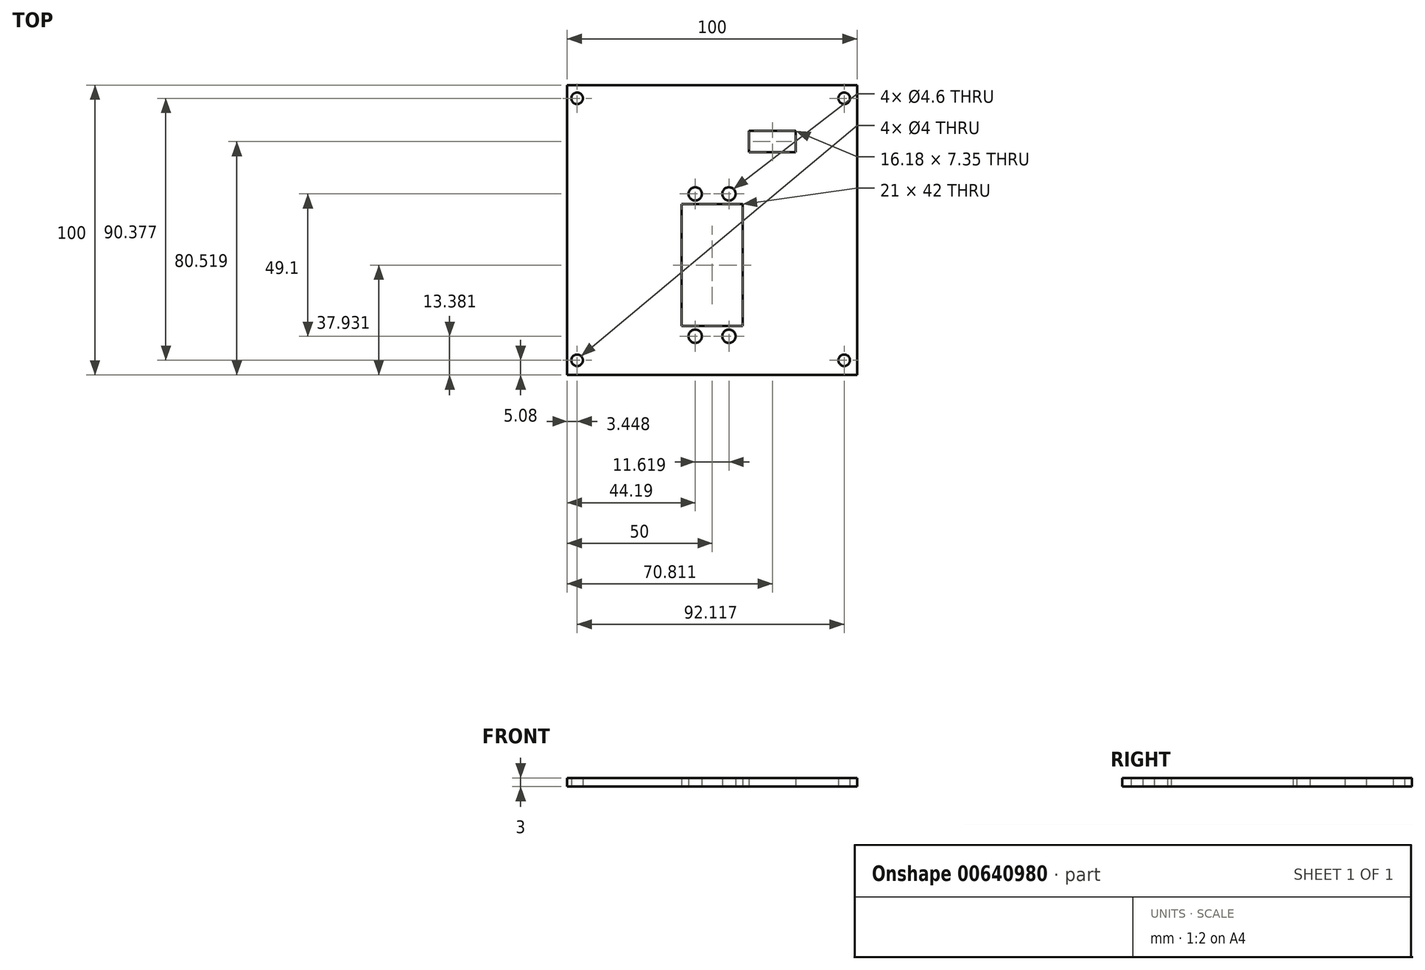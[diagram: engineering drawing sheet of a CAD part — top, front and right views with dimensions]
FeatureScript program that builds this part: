
annotation { "Feature Type Name" : "Feature", "Feature Type Description" : "" }
export const myFeature = defineFeature(function(context is Context, id is Id, definition is map)
    precondition{}
    {
        {
            var Q0;
            Q0=qCreatedBy(makeId("Top.planeOp"),FACE);
            var sketch = newSketch(context, id + "F0", { "sketchPlane" : qUnion([Q0])});
            skLineSegment(sketch, "E0.bottom", {"start": v(50, -50) * mm, "end": v(-50, -50) * mm});
            skLineSegment(sketch, "E0.top", {"start": v(50, 50) * mm, "end": v(-50, 50) * mm});
            skLineSegment(sketch, "E0.left", {"start": v(50, -50) * mm, "end": v(50, 50) * mm});
            skLineSegment(sketch, "E0.right", {"start": v(-50, -50) * mm, "end": v(-50, 50) * mm});
            skPoint(sketch, "E0.middle", {"position": v(0, 11.68) * mm});
            skLineSegment(sketch, "E1.bottom", {"start": v(10.5, -33.07) * mm, "end": v(-10.5, -33.07) * mm});
            skLineSegment(sketch, "E1.top", {"start": v(10.5, 8.93) * mm, "end": v(-10.5, 8.93) * mm});
            skLineSegment(sketch, "E1.left", {"start": v(10.5, -33.07) * mm, "end": v(10.5, 8.93) * mm});
            skLineSegment(sketch, "E1.right", {"start": v(-10.5, -33.07) * mm, "end": v(-10.5, 8.93) * mm});
            skPoint(sketch, "E1.middle", {"position": v(0, -12.07) * mm});
            skCircle(sketch, "E2", {"center": v(-5.8, 12.48) * mm, "radius": 2.3 * mm});
            skCircle(sketch, "E3.MirrorC", {"center": v(5.8, 12.48) * mm, "radius": 2.3 * mm});
            skLineSegment(sketch, "E4", {"start": v(28.9, -12.07) * mm, "end": v(-32.28, -12.07) * mm, "construction": true});
            skCircle(sketch, "E5.MirrorC", {"center": v(-5.8, -36.62) * mm, "radius": 2.3 * mm});
            skCircle(sketch, "E6.MirrorC", {"center": v(5.8, -36.62) * mm, "radius": 2.3 * mm});
            skPoint(sketch, "E7", {"position": v(-46.55, 45.46) * mm});
            skPoint(sketch, "E8.MirrorP", {"position": v(45.56, 45.46) * mm});
            skPoint(sketch, "E9", {"position": v(-46.55, -44.92) * mm});
            skPoint(sketch, "E10.MirrorP", {"position": v(45.56, -44.92) * mm});
            skLineSegment(sketch, "E11", {"start": v(-46.55, 45.46) * mm, "end": v(-46.55, -44.92) * mm, "construction": true});
            skLineSegment(sketch, "E12.bottom", {"start": v(12.72, 34.2) * mm, "end": v(28.9, 34.2) * mm});
            skLineSegment(sketch, "E12.top", {"start": v(12.72, 26.84) * mm, "end": v(28.9, 26.84) * mm});
            skLineSegment(sketch, "E12.left", {"start": v(12.72, 34.2) * mm, "end": v(12.72, 26.84) * mm});
            skLineSegment(sketch, "E12.right", {"start": v(28.9, 34.2) * mm, "end": v(28.9, 26.84) * mm});
            skSolve(sketch);
        }
        {
            var Q0;
            Q0=makeQuery(id+"F0.imprint","IMPRINT",FACE,{"disambiguationData":[TD([[makeQuery(id+"F0.imprint","IMPRINT",EDGE,{"derivedFrom":sQuery(id+"F0.wireOp",EDGE,"E0.bottom")}),-1.0]])]});
            extrude(context, id + "F1", {"entities" : qUnion([Q0]), "depth" : 3 * mm, "offsetDistance" : 25.4 * mm});
        }
        {
            var Q0;
            Q0=sQuery(id+"F0.wireOp",VERTEX,"E7");
            var Q1;
            Q1=sQuery(id+"F0.wireOp",VERTEX,"E8.MirrorP");
            var Q2;
            Q2=sQuery(id+"F0.wireOp",VERTEX,"E10.MirrorP");
            var Q3;
            Q3=sQuery(id+"F0.wireOp",VERTEX,"E9");
            var Q4;
            Q4=makeQuery(id+"F1.opExtrude","SWEPT_BODY",BODY,{"disambiguationData":[OSD([sQuery(id+"F0.wireOp",EDGE,"E0.bottom"),sQuery(id+"F0.wireOp",EDGE,"E0.top"),sQuery(id+"F0.wireOp",EDGE,"E0.left"),sQuery(id+"F0.wireOp",EDGE,"E0.right"),sQuery(id+"F0.wireOp",EDGE,"E1.bottom"),sQuery(id+"F0.wireOp",EDGE,"E1.top"),sQuery(id+"F0.wireOp",EDGE,"E1.left"),sQuery(id+"F0.wireOp",EDGE,"E1.right"),sQuery(id+"F0.wireOp",EDGE,"E2"),sQuery(id+"F0.wireOp",EDGE,"E3.MirrorC"),sQuery(id+"F0.wireOp",EDGE,"E5.MirrorC"),sQuery(id+"F0.wireOp",EDGE,"E6.MirrorC")])]});
            hole(context, id + "F2", {"style" : HoleStyle.SIMPLE, "endStyle" : HoleEndStyle.THROUGH, "oppositeDirection" : true, "holeDiameter" : 4 * mm, "majorDiameter" : 6.35 * mm, "isTappedThrough" : true, "tappedDepth" : 12.7 * mm, "tapClearance" : 3, "locations" : qUnion([Q0, Q1, Q2, Q3]), "scope" : qUnion([Q4])});
        }
    });
